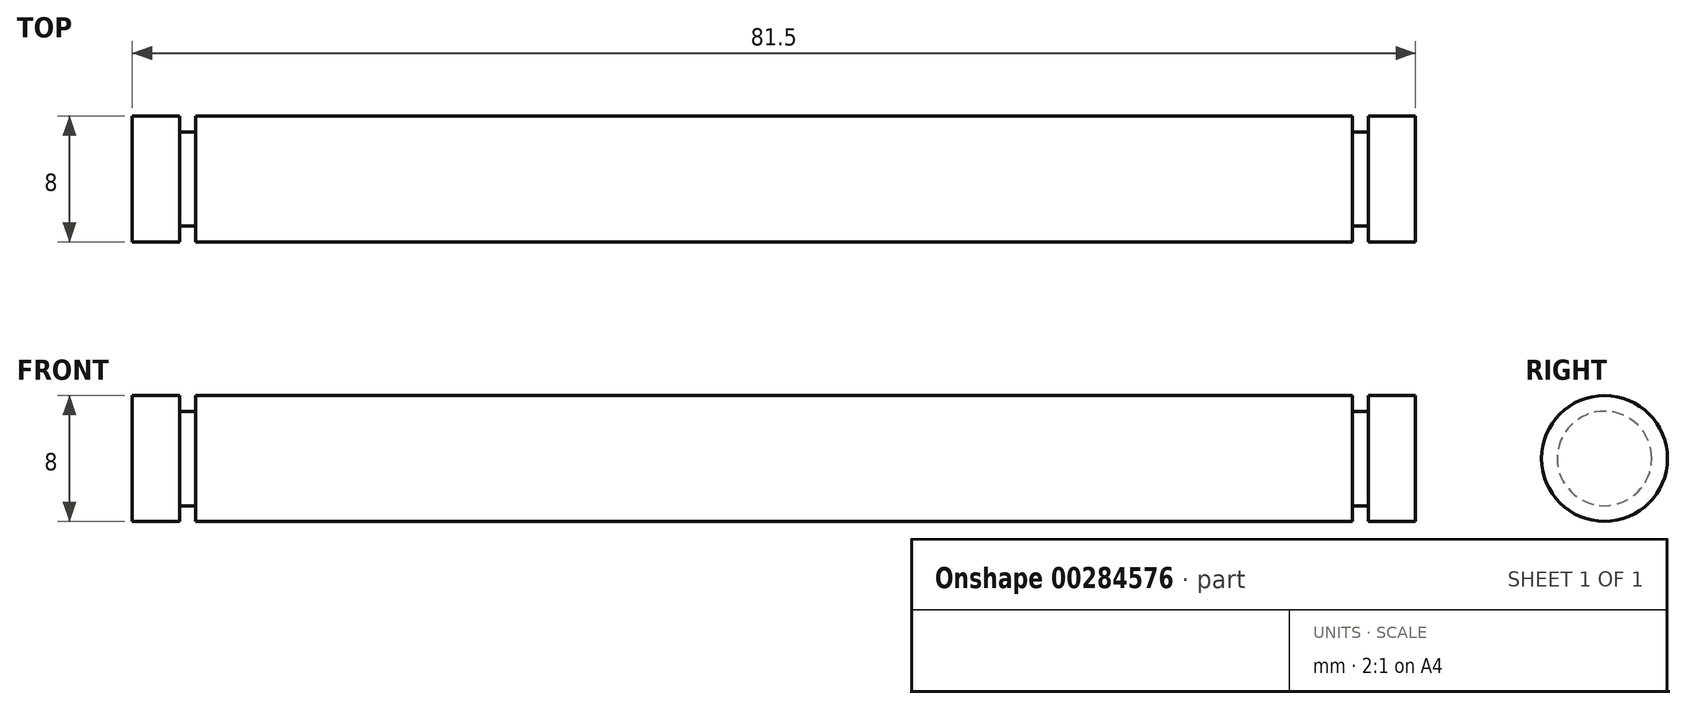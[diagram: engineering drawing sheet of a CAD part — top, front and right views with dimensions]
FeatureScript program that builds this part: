
annotation { "Feature Type Name" : "Feature", "Feature Type Description" : "" }
export const myFeature = defineFeature(function(context is Context, id is Id, definition is map)
    precondition{}
    {
        {
            var Q0;
            Q0=qCreatedBy(makeId("Front.planeOp"),FACE);
            var sketch = newSketch(context, id + "F0", { "sketchPlane" : qUnion([Q0])});
            skLineSegment(sketch, "E0", {"start": v(0, 0) * mm, "end": v(81.5, 0) * mm});
            skLineSegment(sketch, "E1", {"start": v(0, 0) * mm, "end": v(0, 4) * mm});
            skLineSegment(sketch, "E2", {"start": v(0, 4) * mm, "end": v(3, 4) * mm});
            skLineSegment(sketch, "E3", {"start": v(3, 4) * mm, "end": v(3, 3) * mm});
            skLineSegment(sketch, "E4", {"start": v(3, 3) * mm, "end": v(4, 3) * mm});
            skLineSegment(sketch, "E5", {"start": v(4, 3) * mm, "end": v(4, 4) * mm});
            skLineSegment(sketch, "E6", {"start": v(4, 4) * mm, "end": v(77.5, 4) * mm});
            skLineSegment(sketch, "E7", {"start": v(77.5, 4) * mm, "end": v(77.5, 3) * mm});
            skLineSegment(sketch, "E8", {"start": v(77.5, 3) * mm, "end": v(78.5, 3) * mm});
            skLineSegment(sketch, "E9", {"start": v(78.5, 3) * mm, "end": v(78.5, 4) * mm});
            skLineSegment(sketch, "E10", {"start": v(81.5, 0) * mm, "end": v(81.5, 4) * mm});
            skLineSegment(sketch, "E11", {"start": v(81.5, 4) * mm, "end": v(78.5, 4) * mm});
            skSolve(sketch);
        }
        {
            var Q0;
            Q0=qSketchRegion(id+"F0",true);
            var Q1;
            Q1=sQuery(id+"F0.wireOp",EDGE,"E0");
            revolve(context, id + "F1", {"entities" : qUnion([Q0]), "axis" : qUnion([Q1]), "revolveType" : RevolveType.FULL});
        }
    });
